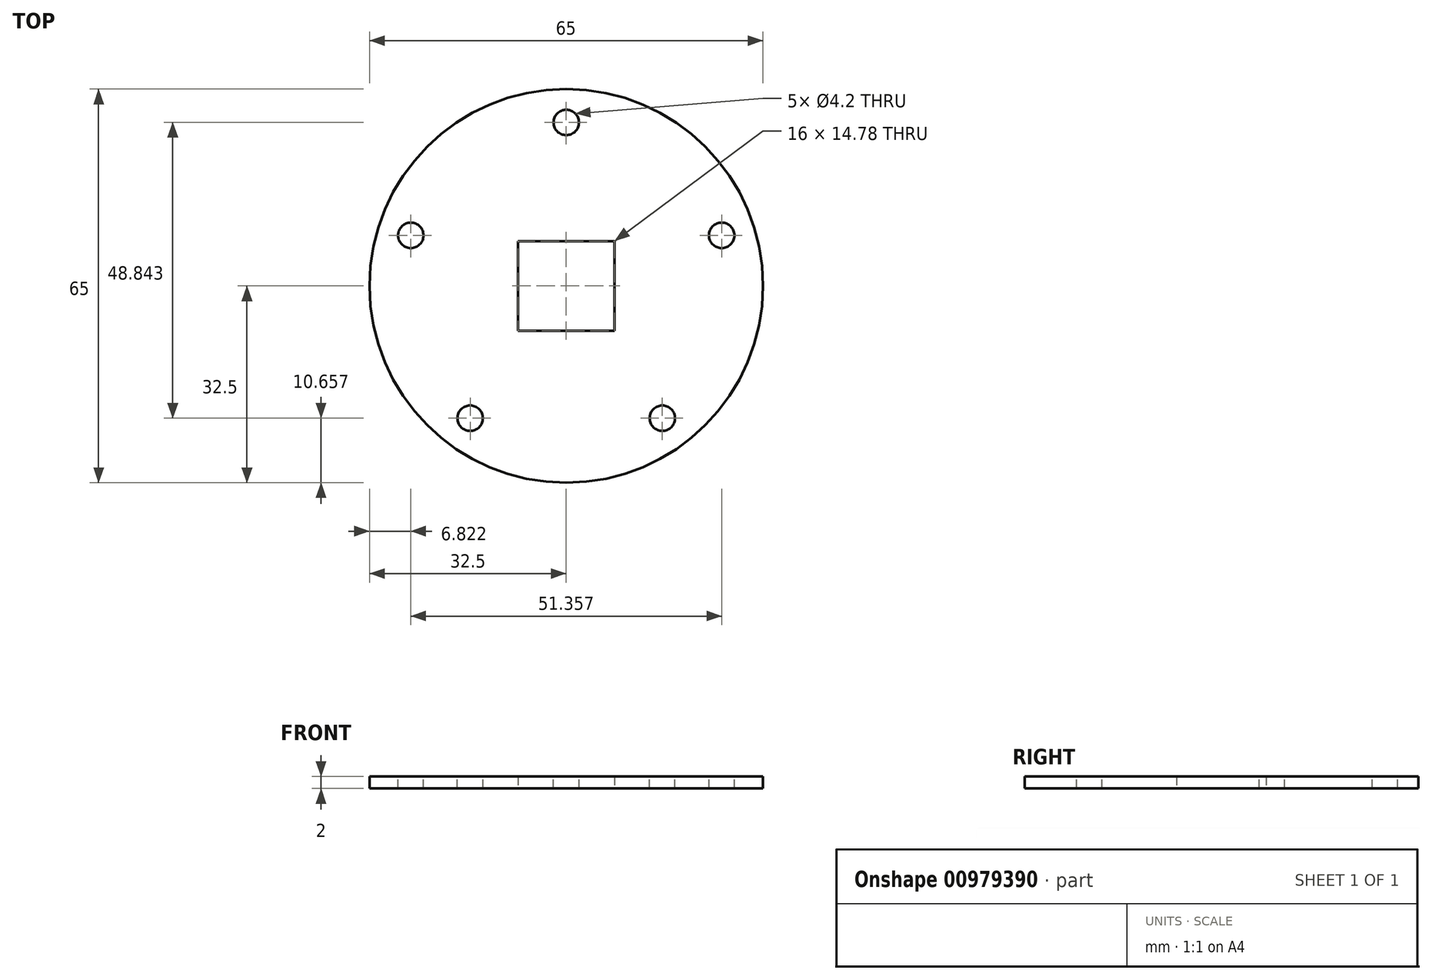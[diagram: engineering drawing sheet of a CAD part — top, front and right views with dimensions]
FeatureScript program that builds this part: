
annotation { "Feature Type Name" : "Feature", "Feature Type Description" : "" }
export const myFeature = defineFeature(function(context is Context, id is Id, definition is map)
    precondition{}
    {
        {
            var Q0;
            Q0=qCreatedBy(makeId("Top.planeOp"),FACE);
            var sketch = newSketch(context, id + "F0", { "sketchPlane" : qUnion([Q0])});
            skCircle(sketch, "E0", {"center": v(0, 0) * mm, "radius": 32.5 * mm});
            skLineSegment(sketch, "E1.bottom", {"start": v(8, -7.39) * mm, "end": v(-8, -7.39) * mm});
            skLineSegment(sketch, "E1.top", {"start": v(8, 7.39) * mm, "end": v(-8, 7.39) * mm});
            skLineSegment(sketch, "E1.left", {"start": v(8, -7.39) * mm, "end": v(8, 7.39) * mm});
            skLineSegment(sketch, "E1.right", {"start": v(-8, -7.39) * mm, "end": v(-8, 7.39) * mm});
            skSolve(sketch);
        }
        {
            var Q0;
            Q0=makeQuery(id+"F0.imprint","IMPRINT",FACE,{"disambiguationData":[TD([[makeQuery(id+"F0.imprint","IMPRINT",EDGE,{"derivedFrom":sQuery(id+"F0.wireOp",EDGE,"E0")}),1.0]])]});
            extrude(context, id + "F1", {"entities" : qUnion([Q0]), "depth" : 2 * mm, "offsetDistance" : 25 * mm});
        }
        {
            var Q0;
            Q0=makeQuery(id+"F1.opExtrude","CAP_FACE",FACE,{"disambiguationData":[OSD([sQuery(id+"F0.wireOp",EDGE,"E0"),sQuery(id+"F0.wireOp",EDGE,"E1.bottom"),sQuery(id+"F0.wireOp",EDGE,"E1.top"),sQuery(id+"F0.wireOp",EDGE,"E1.left"),sQuery(id+"F0.wireOp",EDGE,"E1.right")])],"isStart":false});
            var sketch = newSketch(context, id + "F2", { "sketchPlane" : qUnion([Q0])});
            skCircle(sketch, "E2", {"center": v(0, 27) * mm, "radius": 2.1 * mm});
            skCircle(sketch, "E3.1.0", {"center": v(-25.68, 8.34) * mm, "radius": 2.1 * mm});
            skCircle(sketch, "E3.2.0", {"center": v(-15.87, -21.84) * mm, "radius": 2.1 * mm});
            skCircle(sketch, "E3.3.0", {"center": v(15.87, -21.84) * mm, "radius": 2.1 * mm});
            skCircle(sketch, "E3.4.0", {"center": v(25.68, 8.34) * mm, "radius": 2.1 * mm});
            skPoint(sketch, "E3.center", {"position": v(0, 0) * mm});
            skSolve(sketch);
        }
        {
            var Q0;
            Q0 = qSketchRegion(id + "F2", true);
            extrude(context, id + "F3", {"entities" : qUnion([Q0]), "operationType" : NewBodyOperationType.REMOVE, "endBound" : BoundingType.THROUGH_ALL, "oppositeDirection" : true, "depth" : 25 * mm, "offsetDistance" : 25 * mm});
        }
    });
